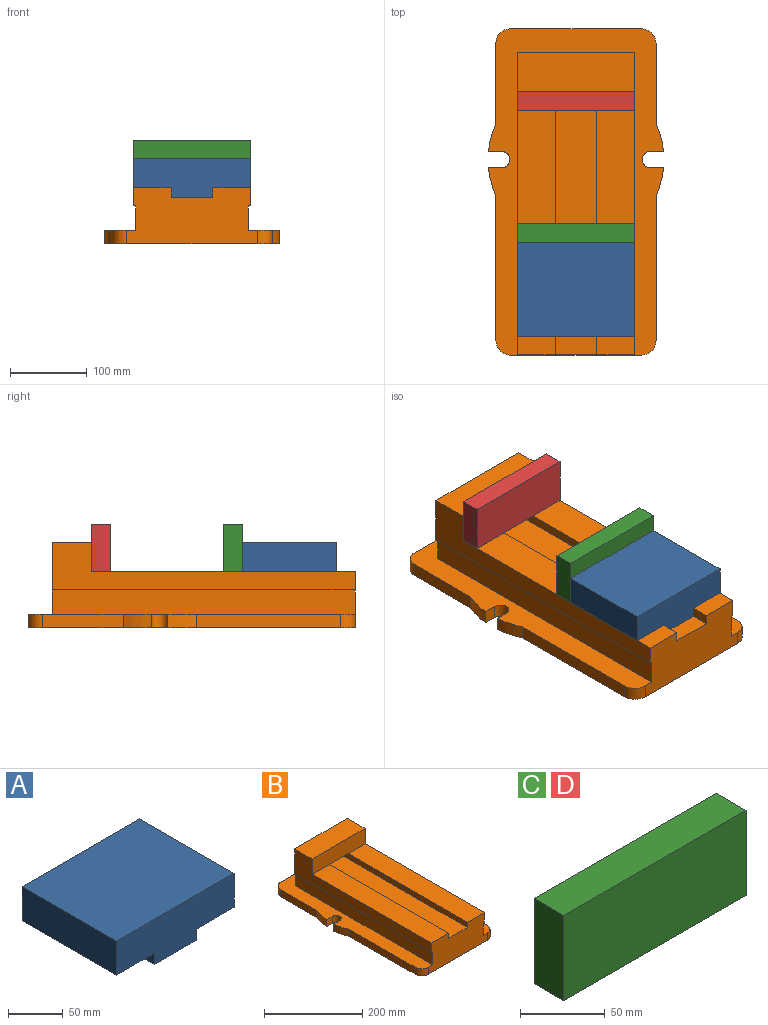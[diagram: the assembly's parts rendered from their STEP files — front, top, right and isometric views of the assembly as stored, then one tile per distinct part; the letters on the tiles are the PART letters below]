
ASSEMBLY  parts=4 mates=6
PART A: 10 faces, bbox 152.4x122.2x50.8 mm
  f0: plane 152.4x122.24mm, normal (0,0,1), area 18629mm2, adj f1,f4,f6,f8
  f1: plane 122.24x38.1mm, normal (1,0,0), area 4657.2mm2, adj f0,f2,f6,f8
  f2: plane 122.24x49.21mm, normal (0,0,-1), area 6015.6mm2, adj f1,f3,f6,f8
  f3: plane 122.24x12.7mm, normal (1,0,0), area 1552.4mm2, adj f2,f5,f6,f8
  f4: plane 122.24x38.1mm, normal (-1,0,0), area 4657.2mm2, adj f0,f6,f7,f8
  f5: plane 122.24x53.98mm, normal (0,0,-1), area 6597.8mm2, adj f3,f6,f8,f9
  f6: plane 152.4x50.8mm, normal (0,-1,0), area 6491.9mm2, adj f0,f1,f2,f3,f4,f5,f7,f9
  f7: plane 122.24x49.21mm, normal (0,0,-1), area 6015.6mm2, adj f4,f6,f8,f9
  f8: plane 152.4x50.8mm, normal (0,1,0), area 6491.9mm2, adj f0,f1,f2,f3,f4,f5,f7,f9
  f9: plane 122.24x12.7mm, normal (-1,0,0), area 1552.4mm2, adj f5,f6,f7,f8
PART B: 37 faces, bbox 227.6x423.9x111.1 mm
  f0: plane 187.5x17.46mm, normal (1,0,0), area 3274.3mm2, adj f1,f18,f19,f21
  f1: cylinder r=114.3mm len=36.77mm, axis (0,0,-1), area 667.7mm2, adj f0,f2,f18,f21
  f2: plane 17.46x16.96mm, normal (0,1,0), area 296.2mm2, adj f1,f3,f18,f21
  f3: cylinder r=10.67mm len=21.35mm, axis (0,0,-1), area 585.5mm2, adj f2,f4,f18,f21
  f4: plane 17.46x16.96mm, normal (0,-1,0), area 296.2mm2, adj f3,f5,f18,f21
  f5: cylinder r=114.3mm len=36.77mm, axis (0,0,-1), area 667.7mm2, adj f4,f6,f18,f21
  f6: plane 103.37x17.46mm, normal (1,0,0), area 1805mm2, adj f5,f7,f18,f21
  f7: cylinder r=19.05mm len=19.05mm, axis (0,0,-1), area 522.5mm2, adj f6,f8,f18,f21
  f8: plane 171.12x17.46mm, normal (0,1,0), area 2988.2mm2, adj f7,f9,f18,f21
  f9: cylinder r=17.81mm len=17.81mm, axis (0,0,-1), area 488.4mm2, adj f8,f10,f18,f21
  f10: plane 104.61x17.46mm, normal (-1,0,0), area 1826.8mm2, adj f9,f11,f18,f21
  f11: cylinder r=114.3mm len=36.77mm, axis (0,0,-1), area 667.7mm2, adj f10,f12,f18,f21
  f12: plane 17.46x16.96mm, normal (0,-1,0), area 296.2mm2, adj f11,f13,f18,f21
  f13: cylinder r=10.67mm len=21.35mm, axis (0,0,-1), area 585.5mm2, adj f12,f14,f18,f21
  f14: plane 17.46x16.96mm, normal (0,1,0), area 296.2mm2, adj f13,f15,f18,f21
  f15: cylinder r=114.3mm len=36.77mm, axis (0,0,-1), area 667.7mm2, adj f14,f16,f18,f21
  f16: plane 187.5x17.46mm, normal (-1,0,0), area 3274.3mm2, adj f15,f17,f18,f21
  f17: cylinder r=19.05mm len=19.05mm, axis (0,0,-1), area 522.5mm2, adj f16,f18,f21,f27
  f18: plane 423.86x227.6mm, normal (0,0,-1), area 88071.8mm2, adj f0,f1,f2,f3,f4,f5,f6,f7
  f19: cylinder r=19.05mm len=19.05mm, axis (0,0,-1), area 522.5mm2, adj f0,f18,f21,f27
  f20: plane 393.7x31.75mm, normal (1,0,0), area 12500mm2, adj f21,f27,f28,f29
  f21: plane 423.86x227.6mm, normal (0,0,1), area 30572mm2, adj f0,f1,f2,f3,f4,f5,f6,f7
  f22: plane 393.7x31.75mm, normal (-1,0,0), area 12500mm2, adj f21,f24,f27,f29
  f23: plane 393.7x53.98mm, normal (0,0,1), area 21250mm2, adj f25,f26,f27,f29
  f24: plane 393.7x3.18mm, normal (0,0,-1), area 1250mm2, adj f22,f27,f29,f31
  f25: plane 393.7x12.7mm, normal (1,0,0), area 5000mm2, adj f23,f27,f29,f32,f33
  f26: plane 393.7x12.7mm, normal (-1,0,0), area 5000mm2, adj f23,f27,f29,f33,f34
  f27: plane 169.88x73.03mm, normal (0,-1,0), area 10547.1mm2, adj f17,f18,f19,f20,f21,f22,f23,f24
  f28: plane 393.7x3.18mm, normal (0,0,-1), area 1250mm2, adj f20,f27,f29,f35
  f29: plane 152.4x93.66mm, normal (0,1,0), area 13387.1mm2, adj f20,f21,f22,f23,f24,f25,f26,f28
  f30: plane 152.4x50.8mm, normal (0,0,1), area 7741.9mm2, adj f29,f31,f35,f36
  f31: plane 393.7x61.91mm, normal (-1,0,0), area 11310.5mm2, adj f24,f27,f29,f30,f32,f36
  f32: plane 342.9x49.21mm, normal (0,0,1), area 16875mm2, adj f25,f27,f31,f36
  f33: plane 53.98x50.8mm, normal (0,0,-1), area 2741.9mm2, adj f25,f26,f29,f36
  f34: plane 342.9x49.21mm, normal (0,0,1), area 16875mm2, adj f26,f27,f35,f36
  f35: plane 393.7x61.91mm, normal (1,0,0), area 11310.5mm2, adj f27,f28,f29,f30,f34,f36
  f36: plane 152.4x38.1mm, normal (0,-1,0), area 5806.4mm2, adj f30,f31,f32,f33,f34,f35
PART C: 6 faces, bbox 152.4x25x61.7 mm
  f0: plane 61.72x25.02mm, normal (-1,0,0), area 1544.2mm2, adj f1,f3,f4,f5
  f1: plane 152.4x25.02mm, normal (0,0,-1), area 3812.9mm2, adj f0,f2,f4,f5
  f2: plane 61.72x25.02mm, normal (1,0,0), area 1544.2mm2, adj f1,f3,f4,f5
  f3: plane 152.4x25.02mm, normal (0,0,1), area 3812.9mm2, adj f0,f2,f4,f5
  f4: plane 152.4x61.72mm, normal (0,-1,0), area 9406.4mm2, adj f0,f1,f2,f3
  f5: plane 152.4x61.72mm, normal (0,1,0), area 9406.4mm2, adj f0,f1,f2,f3
PART D: same geometry as C
PLACE A t=(-417.27,-92.67,259.45)mm
PLACE B t=(-417.27,-41.83,235.64)mm
PLACE C t=(-493.47,-67.66,259.45)mm
PLACE D t=(-493.47,104.22,259.45)mm
MATE planar A.f3 <-> B.f26  axis (1,0,0) through (-390.28,-153.79,253.1)mm
MATE fastened B.f33 <-> D.f1  axis (0,0,1) through (-417.27,104.22,259.45)mm
MATE planar C.f4 <-> A.f8  axis (0,-1,0) through (-417.27,-92.67,290.31)mm
MATE planar B.f32 <-> C.f1  axis (0,0,1) through (-468.86,-67.23,259.45)mm
MATE planar B.f32 <-> A.f7  axis (0,0,1) through (-468.86,-67.23,259.45)mm
MATE planar C.f2 <-> A.f1  axis (1,0,0) through (-341.07,-80.16,290.31)mm
